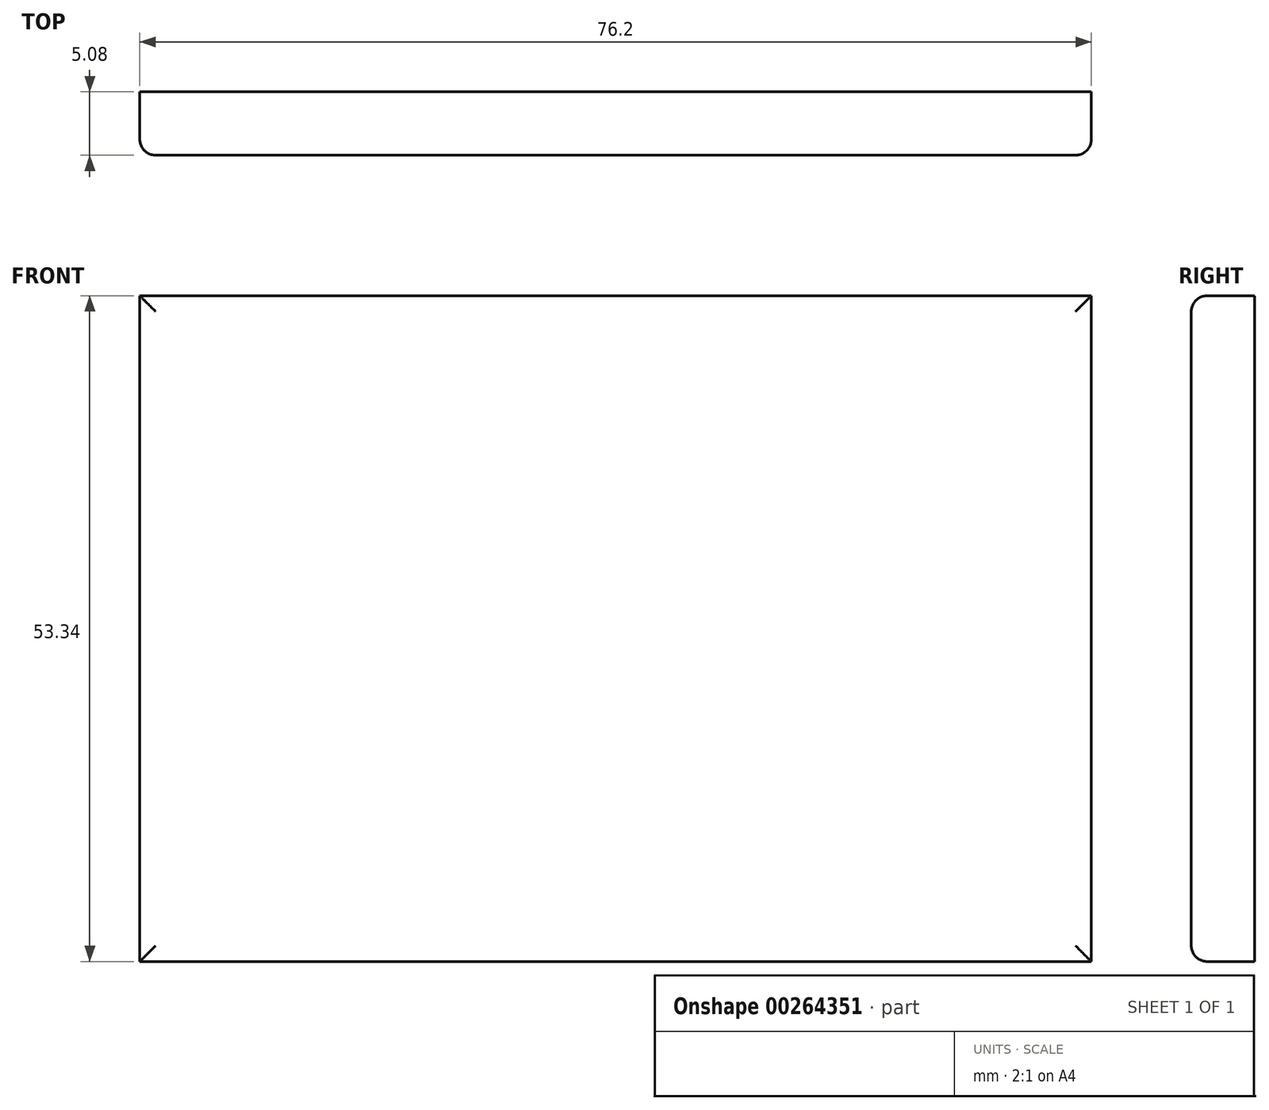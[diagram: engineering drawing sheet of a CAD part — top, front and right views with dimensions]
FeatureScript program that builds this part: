
annotation { "Feature Type Name" : "Feature", "Feature Type Description" : "" }
export const myFeature = defineFeature(function(context is Context, id is Id, definition is map)
    precondition{}
    {
        {
            var Q0;
            Q0=qCreatedBy(makeId("Front.planeOp"),FACE);
            var sketch = newSketch(context, id + "F0", { "sketchPlane" : qUnion([Q0])});
            skLineSegment(sketch, "E0.bottom", {"start": v(38.1, 39.12) * mm, "end": v(-38.1, 39.12) * mm});
            skPoint(sketch, "E0.middle", {"position": v(0, -49.78) * mm});
            skLineSegment(sketch, "E1", {"start": v(-38.1, 39.12) * mm, "end": v(-38.1, -14.22) * mm});
            skLineSegment(sketch, "E2.top", {"start": v(-38.1, -14.22) * mm, "end": v(38.1, -14.22) * mm});
            skLineSegment(sketch, "E2.right", {"start": v(38.1, 39.12) * mm, "end": v(38.1, -14.22) * mm});
            skSolve(sketch);
        }
        {
            var Q0;
            Q0 = qSketchRegion(id + "F0", true);
            extrude(context, id + "F1", {"entities" : qUnion([Q0]), "depth" : 5.08 * mm});
        }
        {
            var Q0;
            Q0=makeQuery(id+"F1.opExtrude","CAP_FACE",FACE,{"disambiguationData":[OSD([sQuery(id+"F0.wireOp",EDGE,"E0.bottom"),sQuery(id+"F0.wireOp",EDGE,"E1"),sQuery(id+"F0.wireOp",EDGE,"E2.top"),sQuery(id+"F0.wireOp",EDGE,"E2.right")])],"isStart":false});
            fillet(context, id + "F2", {"entities" : qUnion([Q0]), "radius" : 1.27 * mm, "tangentPropagation" : true, "allowEdgeOverflow" : false});
        }
    });
